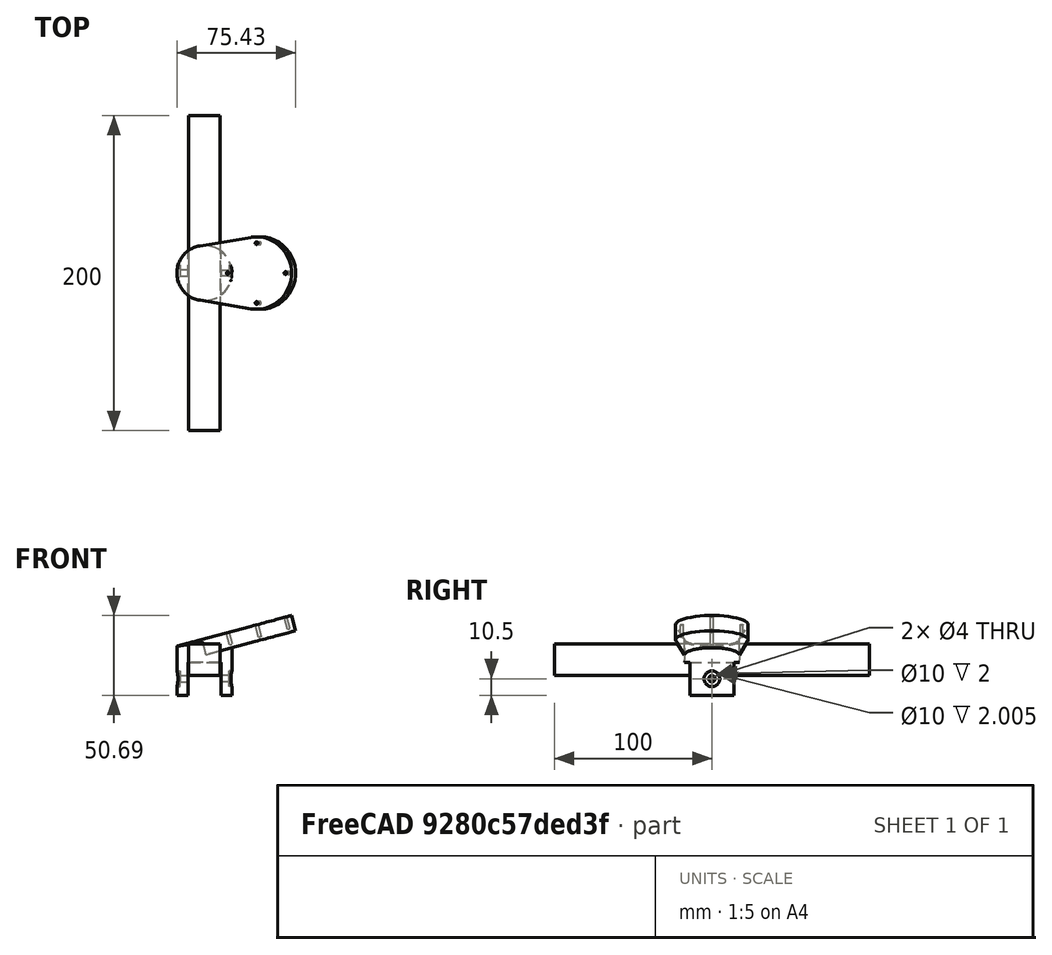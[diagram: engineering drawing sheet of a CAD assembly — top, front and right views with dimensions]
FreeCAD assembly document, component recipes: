
FREECAD ASSEMBLY — COMPONENT RECIPES ("keyboard_chair_attachment_rev2")

This assembly document has 2 components, labeled P0..P1 below (a component is one placed body or linked part). 2 of them carry a construction recipe — the FreeCAD feature program that regenerates the part from scratch, quoted from this document or its linked companion documents; the rest are supplied as boundary geometry only. No exploded tour is included for this assembly.
COMPONENT P0 — recipe-attached ("Extruded Bar", modeled in this document).
Construction recipe (the document's own serialized feature program — sketch geometry with constraints, then the solid features built on it; lengths are millimeters unless a unit is written):

FEATURE [Sketcher::SketchObject] Sketch  label="Extruded Bar Extrusion"
  FullyConstrained = true
  MapMode = 5
  Placement = pos=(0,0,0) rot=(1,0,0;1.5708rad)
  Support = -> [XZ_Plane002]
  expr: Constraints[10] = Variables.extruded_bar_height
  expr: Constraints[11] = Variables.extruded_bar_width
  sketch-geometry (5):
    g0: LineSegment StartX=-10 StartY=-10 StartZ=0 EndX=-10 EndY=10 EndZ=0
    g1: LineSegment StartX=-10 StartY=10 StartZ=0 EndX=10 EndY=10 EndZ=0
    g2: LineSegment StartX=10 StartY=10 StartZ=0 EndX=10 EndY=-10 EndZ=0
    g3: LineSegment StartX=10 StartY=-10 StartZ=0 EndX=-10 EndY=-10 EndZ=0
    g4: GeomPoint X=0 Y=0 Z=0
  constraints (12):
    c: Coincident(g0,g1)
    c: Coincident(g1,g2)
    c: Coincident(g2,g3)
    c: Coincident(g3,g0)
    c: Horizontal(g1)
    c: Horizontal(g3)
    c: Vertical(g0)
    c: Vertical(g2)
    c: Symmetric(g1,g0,g4)
    c: Coincident(g4,g-1)
    c: DistanceY(g2,g2) = 20
    c: DistanceX(g1,g1) = 20
FEATURE [PartDesign::Pad] Pad  label="Extruded Bar Outer"
  Direction = (0,-1,2e-16)
  Length = 200
  Length2 = 10
  Midplane = true
  Placement = pos=(0,0,0) rot=(1,0,0;1.5708rad)
  Profile = -> Sketch
  ReferenceAxis = -> Sketch [N_Axis]
  Type = 0
  expr: Length = Variables.extruded_bar_length
FEATURE [PartDesign::Body] Extruded_Bar_Body  label="Extruded Bar Body"
  Group = -> [Sketch,Pad]
  Origin = -> Origin002
  Tip = -> Pad
COMPONENT P1 — recipe-attached ("Keyboard Mount", modeled in this document).
Construction recipe (the document's own serialized feature program — sketch geometry with constraints, then the solid features built on it; lengths are millimeters unless a unit is written):

FEATURE [PartDesign::CoordinateSystem] LCS_003
  AttacherType = Attacher::AttachEngine3D
  MapMode = 2
  Support = -> [X_Axis004]
FEATURE [Sketcher::SketchObject] Sketch005
  FullyConstrained = true
  MapMode = 5
  Placement = pos=(0,0,0) rot=(1,0,0;1.5708rad)
  Support = -> [XZ_Plane004]
  expr: .Constraints.height = Variables.extruded_bar_height + 1
  expr: .Constraints.width = Variables.extruded_bar_width + 1
  sketch-geometry (5):
    g0: LineSegment StartX=-10.5 StartY=-22.5 StartZ=0 EndX=-10.5 EndY=-1.5 EndZ=0
    g1: LineSegment StartX=-10.5 StartY=-1.5 StartZ=0 EndX=10.5 EndY=-1.5 EndZ=0
    g2: LineSegment StartX=10.5 StartY=-1.5 StartZ=0 EndX=10.5 EndY=-22.5 EndZ=0
    g3: LineSegment StartX=10.5 StartY=-22.5 StartZ=0 EndX=-10.5 EndY=-22.5 EndZ=0
    g4: GeomPoint X=0 Y=-12 Z=0
  constraints (13):
    c: Coincident(g0,g1)
    c: Coincident(g1,g2)
    c: Coincident(g2,g3)
    c: Coincident(g3,g0)
    c: Horizontal(g1)
    c: Horizontal(g3)
    c: Vertical(g0)
    c: Vertical(g2)
    c: Symmetric(g1,g0,g4)
    c: PointOnObject(g4,g-2)
    c: DistanceX(g1,g1) = 21  'width'
    c: DistanceY(g2,g2) = 21  'height'
    c: DistanceY(g4,g-1) = 12  'offset'
FEATURE [PartDesign::Plane] DatumPlane004  label="Keyboard Mount Bar Side Right"
  AttachmentOffset = pos=(0,0,10.5) rot=(0,0,1;0rad)
  Length = 60.1645
  MapMode = 5
  Placement = pos=(10.5,-2.3e-15,2.3e-15) rot=(0.57735,0.57735,0.57735;2.0944rad)
  ResizeMode = 0
  Support = -> [YZ_Plane004]
  Width = 61.8232
  expr: .AttachmentOffset.Base.z = Sketch005.Constraints.width / 2
FEATURE [Sketcher::SketchObject] Sketch006
  FullyConstrained = true
  MapMode = 5
  Placement = pos=(10.5,-2.3e-15,2.3e-15) rot=(0.57735,0.57735,0.57735;2.0944rad)
  Support = -> [DatumPlane004]
  expr: .Constraints.offset = Sketch005.Constraints.offset
  sketch-geometry (1):
    g0: Circle CenterX=0 CenterY=-12 CenterZ=0 NormalX=0 NormalY=0 NormalZ=1 AngleXU=0 Radius=2
  constraints (3):
    c: PointOnObject(g0,g-2)
    c: DistanceY(g0,g-1) = 12  'offset'
    c: Diameter(g0) = 4  'hole_diam'
FEATURE [PartDesign::Plane] DatumPlane005  label="Keyboard Mount Bar Mount Screw Head Right"
  AttachmentOffset = pos=(0,0,5) rot=(0,0,1;0rad)
  Length = 60.1645
  MapMode = 5
  Placement = pos=(15.5,-2.9e-15,2.9e-15) rot=(0.57735,0.57735,0.57735;2.0944rad)
  ResizeMode = 0
  Support = -> [DatumPlane004]
  Width = 61.8232
FEATURE [Sketcher::SketchObject] Sketch007
  FullyConstrained = true
  MapMode = 5
  Placement = pos=(15.5,-2.9e-15,2.9e-15) rot=(0.57735,0.57735,0.57735;2.0944rad)
  Support = -> [DatumPlane005]
  expr: .Constraints.offset = Sketch005.Constraints.offset
  sketch-geometry (1):
    g0: Circle CenterX=0 CenterY=-12 CenterZ=0 NormalX=0 NormalY=0 NormalZ=1 AngleXU=0 Radius=5
  constraints (3):
    c: PointOnObject(g0,g-2)
    c: DistanceY(g0,g-1) = 12  'offset'
    c: Diameter(g0) = 10  'hole_diam'
FEATURE [PartDesign::CoordinateSystem] Local_CS  label="Keyboard Mount Body Bar"
  AttacherType = Attacher::AttachEngine3D
  AttachmentOffset = pos=(0,0,-12) rot=(0,0,1;0rad)
  MapMode = 5
  Placement = pos=(0,0,-12) rot=(0,0,1;0rad)
  Support = -> [LCS_003]
  expr: .AttachmentOffset.Base.z = -Sketch005.Constraints.offset
FEATURE [PartDesign::Plane] DatumPlane006  label="Keyboard Mount Bar Side Left"
  AttachmentOffset = pos=(0,0,-10.5) rot=(0,0,1;0rad)
  Length = 60.1645
  MapMode = 5
  Placement = pos=(-10.5,2.3e-15,-2.3e-15) rot=(0.57735,0.57735,0.57735;2.0944rad)
  ResizeMode = 0
  Support = -> [YZ_Plane004]
  Width = 61.8232
  expr: .AttachmentOffset.Base.z = -Sketch005.Constraints.width / 2
FEATURE [PartDesign::Plane] DatumPlane007  label="Keyboard Mount Bar Mount Screw Head Left"
  AttachmentOffset = pos=(0,0,-5) rot=(0,0,1;0rad)
  Length = 60.1645
  MapMode = 5
  Placement = pos=(-15.5,2.9e-15,-2.9e-15) rot=(0.57735,0.57735,0.57735;2.0944rad)
  ResizeMode = 0
  Support = -> [DatumPlane006]
  Width = 61.8232
FEATURE [Sketcher::SketchObject] Sketch008
  FullyConstrained = true
  MapMode = 5
  Placement = pos=(-10.5,2.3e-15,-2.3e-15) rot=(0.57735,0.57735,0.57735;2.0944rad)
  Support = -> [DatumPlane006]
  expr: Constraints[1] = Sketch006.Constraints.hole_diam
  expr: Constraints[2] = Sketch006.Constraints.offset
  sketch-geometry (1):
    g0: Circle CenterX=0 CenterY=-12 CenterZ=0 NormalX=0 NormalY=0 NormalZ=1 AngleXU=0 Radius=2
  constraints (3):
    c: PointOnObject(g0,g-2)
    c: Diameter(g0) = 4
    c: DistanceY(g0,g-1) = 12
FEATURE [Sketcher::SketchObject] Sketch009
  FullyConstrained = true
  MapMode = 5
  Placement = pos=(-15.5,2.9e-15,-2.9e-15) rot=(0.57735,0.57735,0.57735;2.0944rad)
  Support = -> [DatumPlane007]
  expr: Constraints[1] = Sketch007.Constraints.offset
  expr: Constraints[2] = Sketch007.Constraints.hole_diam
  sketch-geometry (1):
    g0: Circle CenterX=0 CenterY=-12 CenterZ=0 NormalX=0 NormalY=0 NormalZ=1 AngleXU=0 Radius=5
  constraints (3):
    c: PointOnObject(g0,g-2)
    c: DistanceY(g0,g-1) = 12
    c: Diameter(g0) = 10
FEATURE [PartDesign::Plane] DatumPlane010  label="Keyboard Mount Bar Mount Top"
  Length = 94.4443
  MapMode = 5
  ResizeMode = 0
  Support = -> [XY_Plane004]
  Width = 62.78
FEATURE [PartDesign::Plane] DatumPlane011  label="Keyboard Mount Bar Mount Bottom"
  AttachmentOffset = pos=(0,0,-22.5) rot=(0,0,1;0rad)
  Length = 94.4443
  MapMode = 5
  Placement = pos=(0,0,-22.5) rot=(0,0,1;0rad)
  ResizeMode = 0
  Support = -> [DatumPlane010]
  Width = 62.78
  expr: .AttachmentOffset.Base.z = -<<Sketch005>>.Constraints.offset - Sketch005.Constraints.height / 2
FEATURE [Sketcher::SketchObject] Sketch011
  FullyConstrained = true
  MapMode = 5
  Support = -> [DatumPlane010]
  sketch-geometry (1):
    g0: Circle CenterX=0 CenterY=0 CenterZ=0 NormalX=0 NormalY=0 NormalZ=1 AngleXU=0 Radius=17.5
  constraints (2):
    c: Coincident(g0,g-1)
    c: Diameter(g0) = 35  'diam'
FEATURE [PartDesign::CoordinateSystem] Local_CS001  label="Keyboard Mount Edge Position"
  AttacherType = Attacher::AttachEngine3D
  AttachmentOffset = pos=(-20,0,8) rot=(0,0,1;0rad)
  MapMode = 5
  Placement = pos=(-20,0,8) rot=(0,0,1;0rad)
  Support = -> [XY_Plane004]
FEATURE [PartDesign::Plane] DatumPlane  label="Keyboard Mount Tenting Puck Support Top Angle"
  AttachmentOffset = pos=(0,0,0) rot=(0,-1,0;0.261799rad)
  Length = 105.835
  MapMode = 5
  Placement = pos=(-20,0,8) rot=(0,-1,0;0.261799rad)
  ResizeMode = 0
  Support = -> [Local_CS001]
  Width = 63.5832
FEATURE [PartDesign::Plane] DatumPlane012  label="Keyboard Mount Tenting Puck Support Top"
  AttachmentOffset = pos=(55,0,0) rot=(0,0,1;0rad)
  Length = 105.835
  MapMode = 5
  Placement = pos=(33.1259,0,22.235) rot=(0,-1,0;0.261799rad)
  ResizeMode = 0
  Support = -> [DatumPlane]
  Width = 63.5832
FEATURE [Sketcher::SketchObject] Sketch012
  FullyConstrained = true
  MapMode = 5
  Placement = pos=(33.1259,0,22.235) rot=(0,-1,0;0.261799rad)
  Support = -> [DatumPlane012]
  sketch-geometry (5):
    g0: Circle CenterX=0 CenterY=0 CenterZ=0 NormalX=0 NormalY=0 NormalZ=1 AngleXU=0 Radius=19
    g1: Circle CenterX=0 CenterY=19 CenterZ=0 NormalX=0 NormalY=0 NormalZ=1 AngleXU=0 Radius=0.85
    g2: Circle CenterX=-19 CenterY=0 CenterZ=0 NormalX=0 NormalY=0 NormalZ=1 AngleXU=0 Radius=0.85
    g3: Circle CenterX=19 CenterY=0 CenterZ=0 NormalX=0 NormalY=0 NormalZ=1 AngleXU=0 Radius=0.85
    g4: Circle CenterX=0 CenterY=-19 CenterZ=0 NormalX=0 NormalY=0 NormalZ=1 AngleXU=0 Radius=0.85
  constraints (14):
    c: Coincident(g0,g-1)
    c: PointOnObject(g1,g0)
    c: PointOnObject(g2,g0)
    c: PointOnObject(g3,g0)
    c: PointOnObject(g4,g0)
    c: PointOnObject(g4,g-2)
    c: Tangent(g1,g-2) = -1.5708
    c: PointOnObject(g2,g-1)
    c: PointOnObject(g3,g-1)
    c: Equal(g1,g2)
    c: Equal(g2,g3)
    c: Equal(g3,g4)
    c: Diameter(g1) = 1.7
    c: Diameter(g0) = 38  'hole_centres'
FEATURE [PartDesign::Plane] DatumPlane013  label="Keyboard Mount Tenting Puck Support Bottom"
  AttachmentOffset = pos=(0,0,-10) rot=(0,0,1;0rad)
  Length = 105.835
  MapMode = 5
  Placement = pos=(35.7141,0,12.5758) rot=(0,-1,0;0.261799rad)
  ResizeMode = 0
  Support = -> [DatumPlane012]
  Width = 63.5832
FEATURE [Sketcher::SketchObject] Sketch013
  FullyConstrained = true
  MapMode = 5
  Support = -> [DatumPlane010]
  expr: Constraints[1] = Sketch011.Constraints.diam
  sketch-geometry (1):
    g0: Circle CenterX=0 CenterY=0 CenterZ=0 NormalX=0 NormalY=0 NormalZ=1 AngleXU=0 Radius=17.5
  constraints (2):
    c: Coincident(g0,g-1)
    c: Diameter(g0) = 35
FEATURE [PartDesign::Pad] Pad003  label="Keyboard Mount Bar Padding"
  Direction = (0,0,1)
  Length = 10
  Length2 = 10
  Profile = -> Sketch013
  ReferenceAxis = -> Sketch013 [N_Axis]
  Type = 3
  UpToFace = -> DatumPlane012 [Plane]
FEATURE [PartDesign::Pad] Pad002  label="Keyboard Mount Bar Mount"
  BaseFeature = -> Pad003
  Direction = (0,0,1)
  Length = 10
  Length2 = 10
  Profile = -> Sketch011
  ReferenceAxis = -> Sketch011 [N_Axis]
  Type = 3
  UpToFace = -> DatumPlane011 [Plane]
FEATURE [Sketcher::SketchObject] Sketch014
  ExternalGeometry = -> [Pad002]
  FullyConstrained = true
  MapMode = 5
  Placement = pos=(33.1259,0,22.235) rot=(0,-1,0;0.261799rad)
  Support = -> [DatumPlane012]
  sketch-geometry (6):
    g0: GeomPoint X=-52.4118 Y=0 Z=0
    g1: Circle CenterX=0 CenterY=0 CenterZ=0 NormalX=0 NormalY=0 NormalZ=1 AngleXU=0 Radius=23
    g2: LineSegment StartX=-37.291 StartY=17.259 StartZ=0 EndX=-3.67787 EndY=22.704 EndZ=0
    g3: LineSegment StartX=-37.291 StartY=-17.259 StartZ=0 EndX=-3.67787 EndY=-22.704 EndZ=0
    g4: ArcOfCircle CenterX=1.8e-15 CenterY=1e-15 CenterZ=0 NormalX=0 NormalY=0 NormalZ=1 AngleXU=0 Radius=23 StartAngle=4.55179 EndAngle=8.01458
    g5: ArcOfCircle CenterX=-35.0017 CenterY=3.2e-15 CenterZ=0 NormalX=0 NormalY=0 NormalZ=1 AngleXU=0 Radius=17.4102 StartAngle=1.70267 EndAngle=4.58051
  constraints (14):
    c: Coincident(g1,g-1)
    c: Diameter(g1) = 46  'diam'
    c: Coincident(g4,g2)
    c: Coincident(g4,g3)
    c: Tangent(g4,g1)
    c: Coincident(g5,g2)
    c: Coincident(g5,g3)
    c: PointOnObject(g0,g5)
    c: Tangent(g2,g1) = 1.5708
    c: Tangent(g3,g1) = -1.5708
    c: PointOnObject(g0,g-1)
    c: Tangent(g2,g-3) = 1.5708
    c: Tangent(g3,g-3) = -1.5708
    c: PointOnObject(g0,g-3)
FEATURE [PartDesign::Pad] Pad004  label="Keyboard Mount Tenting Puck Support"
  BaseFeature = -> Pad002
  Direction = (-0.258819,0,0.965926)
  Length = 10
  Length2 = 10
  Profile = -> Sketch014
  ReferenceAxis = -> Sketch014 [N_Axis]
  Type = 3
  UpToFace = -> DatumPlane013
FEATURE [PartDesign::Plane] DatumPlane014  label="Keyboard Mount Tenting Puck Hole Depth"
  AttachmentOffset = pos=(0,0,-8) rot=(0,0,1;0rad)
  Length = 105.835
  MapMode = 5
  Placement = pos=(35.1965,0,14.5076) rot=(0,-1,0;0.261799rad)
  ResizeMode = 0
  Support = -> [DatumPlane012]
  Width = 63.5832
FEATURE [PartDesign::Pocket] Pocket  label="Keyboard Mount Tenting Puck Holes"
  BaseFeature = -> Pad004
  Direction = (0.258819,0,-0.965926)
  Length = 0
  Length2 = 5
  Profile = -> Sketch012
  ReferenceAxis = -> Sketch012 [N_Axis]
  Type = 3
  UpToFace = -> DatumPlane014 [Plane]
FEATURE [PartDesign::Pocket] Pocket001  label="Keyboard Mount Bar Cutout"
  BaseFeature = -> Pocket
  Direction = (0,1,2e-16)
  Length = 5
  Length2 = 5
  Midplane = true
  Profile = -> Sketch005
  ReferenceAxis = -> Sketch005 [N_Axis]
  Type = 1
FEATURE [PartDesign::Pocket] Pocket002  label="Keyboard Mount Bar Screw Cutout Right"
  BaseFeature = -> Pocket001
  Direction = (-1,1e-16,-1e-16)
  Length = 5
  Length2 = 5
  Profile = -> Sketch006
  ReferenceAxis = -> Sketch006 [N_Axis]
  Reversed = true
  Type = 1
FEATURE [PartDesign::Pocket] Pocket003  label="Keyboard Mount Bar Screw Head Cutout Right"
  BaseFeature = -> Pocket002
  Direction = (-1,0,0)
  Length = 5
  Length2 = 5
  Profile = -> Sketch007
  ReferenceAxis = -> Sketch007 [N_Axis]
  Reversed = true
  Type = 1
FEATURE [PartDesign::Pocket] Pocket004  label="Keyboard Mount Bar Screw Cutout Left"
  BaseFeature = -> Pocket003
  Direction = (-1,1e-16,-1e-16)
  Length = 5
  Length2 = 5
  Profile = -> Sketch008
  ReferenceAxis = -> Sketch008 [N_Axis]
  Type = 1
FEATURE [PartDesign::Pocket] Pocket005  label="Keyboard Mount Bar Screw Head Cutout Left"
  BaseFeature = -> Pocket004
  Direction = (-1,0,0)
  Length = 0
  Length2 = 5
  Profile = -> Sketch009
  ReferenceAxis = -> Sketch009 [N_Axis]
  Type = 1
FEATURE [PartDesign::Body] Keyboard_Mount_Body  label="Keyboard Mount Body"
  Group = -> [LCS_003,DatumPlane010,Pad003,DatumPlane011,Pad002,Local_CS001,DatumPlane,DatumPlane012,DatumPlane014,DatumPlane013,Pad004,Pocket,Sketch012,Sketch005,Pocket001,DatumPlane004,Sketch006,Pocket002,DatumPlane005,Sketch007,Pocket003,Local_CS,DatumPlane006,Sketch008,Pocket004,DatumPlane007,Sketch009,Pocket005,Sketch011,Sketch013,Sketch014]
  Origin = -> Origin004
  Tip = -> Pocket005
PROVENANCE & LICENSES
A FreeCAD (.FCStd) document from a public repository crawl; recipes are the document's own serialized feature recipes (and, for linked parts, companion documents' recipes).
License: as declared in the source repository (recorded in the dataset sidecar).
